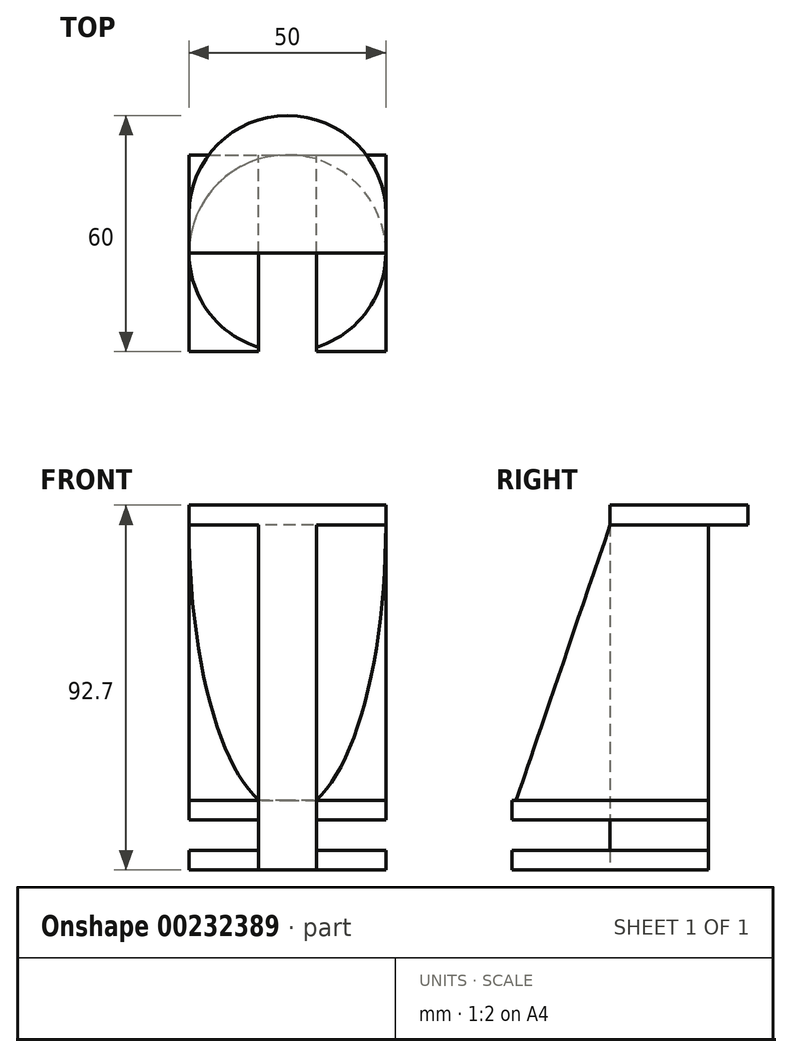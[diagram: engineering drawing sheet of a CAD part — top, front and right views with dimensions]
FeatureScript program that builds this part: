
annotation { "Feature Type Name" : "Feature", "Feature Type Description" : "" }
export const myFeature = defineFeature(function(context is Context, id is Id, definition is map)
    precondition{}
    {
        {
            var Q0;
            Q0=qCreatedBy(makeId("Top.planeOp"),FACE);
            var sketch = newSketch(context, id + "F0", { "sketchPlane" : qUnion([Q0])});
            skLineSegment(sketch, "E0.bottom", {"start": v(0, 0) * mm, "end": v(50, 0) * mm, "construction": true});
            skLineSegment(sketch, "E0.top", {"start": v(0, 50) * mm, "end": v(50, 50) * mm, "construction": true});
            skLineSegment(sketch, "E0.left", {"start": v(0, 0) * mm, "end": v(0, 50) * mm, "construction": true});
            skLineSegment(sketch, "E0.right", {"start": v(50, 0) * mm, "end": v(50, 50) * mm, "construction": true});
            skLineSegment(sketch, "E1.bottom", {"start": v(17.65, 50) * mm, "end": v(32.35, 50) * mm, "construction": true});
            skLineSegment(sketch, "E1.top", {"start": v(17.65, 25) * mm, "end": v(32.35, 25) * mm, "construction": true});
            skLineSegment(sketch, "E1.left", {"start": v(17.65, 50) * mm, "end": v(17.65, 25) * mm, "construction": true});
            skLineSegment(sketch, "E1.right", {"start": v(32.35, 50) * mm, "end": v(32.35, 25) * mm, "construction": true});
            skSolve(sketch);
        }
        {
            var Q0;
            Q0=qCreatedBy(makeId("Top.planeOp"),FACE);
            var sketch = newSketch(context, id + "F1", { "sketchPlane" : qUnion([Q0])});
            skLineSegment(sketch, "E2.0", {"start": v(0, 0) * mm, "end": v(0, 50) * mm});
            skLineSegment(sketch, "E3.0", {"start": v(0, 50) * mm, "end": v(50, 50) * mm});
            skLineSegment(sketch, "E4.0", {"start": v(50, 0) * mm, "end": v(50, 50) * mm});
            skLineSegment(sketch, "E5.0", {"start": v(17.65, 50) * mm, "end": v(17.65, 25) * mm, "construction": true});
            skLineSegment(sketch, "E6.0", {"start": v(17.65, 25) * mm, "end": v(32.35, 25) * mm, "construction": true});
            skLineSegment(sketch, "E7.0", {"start": v(32.35, 50) * mm, "end": v(32.35, 25) * mm, "construction": true});
            skLineSegment(sketch, "E8.0", {"start": v(0, 0) * mm, "end": v(50, 0) * mm, "construction": true});
            skLineSegment(sketch, "E9", {"start": v(0, 0) * mm, "end": v(17.65, 0) * mm});
            skLineSegment(sketch, "E10", {"start": v(17.65, 0) * mm, "end": v(17.65, 25) * mm});
            skLineSegment(sketch, "E11", {"start": v(32.35, 25) * mm, "end": v(32.35, 0) * mm});
            skLineSegment(sketch, "E12", {"start": v(32.35, 0) * mm, "end": v(50, 0) * mm});
            skLineSegment(sketch, "E13", {"start": v(17.65, 25) * mm, "end": v(32.35, 25) * mm});
            skSolve(sketch);
        }
        {
            var Q0;
            Q0 = qSketchRegion(id + "F1", true);
            extrude(context, id + "F2", {"entities" : qUnion([Q0]), "depth" : 5 * mm});
        }
        {
            var Q0;
            Q0=makeQuery(id+"F2.opExtrude","CAP_FACE",FACE,{"disambiguationData":[OSD([sQuery(id+"F1.wireOp",EDGE,"E2.0"),sQuery(id+"F1.wireOp",EDGE,"E3.0"),sQuery(id+"F1.wireOp",EDGE,"E4.0"),sQuery(id+"F1.wireOp",EDGE,"E9"),sQuery(id+"F1.wireOp",EDGE,"E10"),sQuery(id+"F1.wireOp",EDGE,"E11"),sQuery(id+"F1.wireOp",EDGE,"E12"),sQuery(id+"F1.wireOp",EDGE,"E13")])],"isStart":false});
            var sketch = newSketch(context, id + "F3", { "sketchPlane" : qUnion([Q0])});
            skLineSegment(sketch, "E14.bottom", {"start": v(17.65, 25) * mm, "end": v(32.35, 25) * mm});
            skLineSegment(sketch, "E14.top", {"start": v(17.65, 50) * mm, "end": v(32.35, 50) * mm});
            skLineSegment(sketch, "E14.left", {"start": v(17.65, 25) * mm, "end": v(17.65, 50) * mm});
            skLineSegment(sketch, "E14.right", {"start": v(32.35, 25) * mm, "end": v(32.35, 50) * mm});
            skSolve(sketch);
        }
        {
            var Q0;
            Q0 = qSketchRegion(id + "F3", true);
            extrude(context, id + "F4", {"entities" : qUnion([Q0]), "operationType" : NewBodyOperationType.ADD, "depth" : 7.7 * mm});
        }
        {
            var Q0;
            Q0=makeQuery(id+"F4.opExtrude","CAP_FACE",FACE,{"disambiguationData":[OSD([sQuery(id+"F3.wireOp",EDGE,"E14.bottom"),sQuery(id+"F3.wireOp",EDGE,"E14.top"),sQuery(id+"F3.wireOp",EDGE,"E14.left"),sQuery(id+"F3.wireOp",EDGE,"E14.right")])],"isStart":false});
            var sketch = newSketch(context, id + "F5", { "sketchPlane" : qUnion([Q0])});
            skLineSegment(sketch, "E15.0", {"start": v(0, 0) * mm, "end": v(0, 50) * mm});
            skLineSegment(sketch, "E16.0", {"start": v(0, 50) * mm, "end": v(50, 50) * mm});
            skLineSegment(sketch, "E17.0", {"start": v(50, 0) * mm, "end": v(50, 50) * mm});
            skLineSegment(sketch, "E18.0", {"start": v(32.35, 25) * mm, "end": v(32.35, 0) * mm});
            skLineSegment(sketch, "E19.0", {"start": v(17.65, 25) * mm, "end": v(32.35, 25) * mm});
            skLineSegment(sketch, "E20.0", {"start": v(17.65, 0) * mm, "end": v(17.65, 25) * mm});
            skLineSegment(sketch, "E21", {"start": v(0, 0) * mm, "end": v(17.65, 0) * mm});
            skLineSegment(sketch, "E22", {"start": v(32.35, 0) * mm, "end": v(50, 0) * mm});
            skSolve(sketch);
        }
        {
            var Q0;
            Q0 = qSketchRegion(id + "F5", true);
            extrude(context, id + "F6", {"entities" : qUnion([Q0]), "operationType" : NewBodyOperationType.ADD, "depth" : 5 * mm});
        }
        {
            var Q0;
            Q0=makeQuery(id+"F6.opExtrude","CAP_FACE",FACE,{"disambiguationData":[OSD([sQuery(id+"F5.wireOp",EDGE,"E15.0"),sQuery(id+"F5.wireOp",EDGE,"E16.0"),sQuery(id+"F5.wireOp",EDGE,"E17.0"),sQuery(id+"F5.wireOp",EDGE,"E18.0"),sQuery(id+"F5.wireOp",EDGE,"E19.0"),sQuery(id+"F5.wireOp",EDGE,"E20.0"),sQuery(id+"F5.wireOp",EDGE,"E21"),sQuery(id+"F5.wireOp",EDGE,"E22")])],"isStart":false});
            var sketch = newSketch(context, id + "F7", { "sketchPlane" : qUnion([Q0])});
            skArc(sketch, "E23", {"start": v(32.35, 1.1) * mm, "mid": v(25, 50) * mm, "end": v(17.65, 1.1) * mm});
            skLineSegment(sketch, "E24.0", {"start": v(17.65, 25) * mm, "end": v(32.35, 25) * mm});
            skLineSegment(sketch, "E25.0", {"start": v(17.65, 1.1) * mm, "end": v(17.65, 25) * mm});
            skLineSegment(sketch, "E26.0", {"start": v(32.35, 25) * mm, "end": v(32.35, 1.1) * mm});
            skPoint(sketch, "E27.orphan", {"position": v(32.35, 0) * mm});
            skPoint(sketch, "E28.orphan", {"position": v(17.65, 0) * mm});
            skSolve(sketch);
        }
        {
            var Q0;
            Q0 = qSketchRegion(id + "F7", true);
            extrude(context, id + "F8", {"entities" : qUnion([Q0]), "operationType" : NewBodyOperationType.ADD, "depth" : 70 * mm});
        }
        {
            var Q0;
            Q0=makeQuery(id+"F8.opExtrude","CAP_FACE",FACE,{"disambiguationData":[OSD([sQuery(id+"F7.wireOp",EDGE,"E23"),sQuery(id+"F7.wireOp",EDGE,"E24.0"),sQuery(id+"F7.wireOp",EDGE,"E25.0"),sQuery(id+"F7.wireOp",EDGE,"E26.0")])],"isStart":false});
            var sketch = newSketch(context, id + "F9", { "sketchPlane" : qUnion([Q0])});
            skLineSegment(sketch, "E29.bottom", {"start": v(0, 25) * mm, "end": v(50, 25) * mm});
            skLineSegment(sketch, "E29.left", {"start": v(0, 25) * mm, "end": v(0, 35) * mm});
            skLineSegment(sketch, "E29.right", {"start": v(50, 25) * mm, "end": v(50, 35) * mm});
            skArc(sketch, "E30.trimOffspring", {"start": v(50, 35) * mm, "mid": v(25, 60) * mm, "end": v(0, 35) * mm});
            skSolve(sketch);
        }
        {
            var Q0;
            Q0 = qSketchRegion(id + "F9", true);
            extrude(context, id + "F10", {"entities" : qUnion([Q0]), "operationType" : NewBodyOperationType.ADD, "depth" : 5 * mm});
        }
        {
            var Q0;
            Q0=qCreatedBy(makeId("Right.planeOp"),FACE);
            var sketch = newSketch(context, id + "F11", { "sketchPlane" : qUnion([Q0])});
            skLineSegment(sketch, "E31.0", {"start": v(1.1, 87.7) * mm, "end": v(1.1, 17.7) * mm, "construction": true});
            skLineSegment(sketch, "E32.0", {"start": v(25, 87.7) * mm, "end": v(1.1, 87.7) * mm});
            skLineSegment(sketch, "E33", {"start": v(1.1, 17.7) * mm, "end": v(25, 87.7) * mm});
            skLineSegment(sketch, "E34", {"start": v(1.1, 87.7) * mm, "end": v(1.1, 17.7) * mm});
            skSolve(sketch);
        }
        {
            var Q0;
            Q0 = qSketchRegion(id + "F11", true);
            extrude(context, id + "F12", {"entities" : qUnion([Q0]), "operationType" : NewBodyOperationType.REMOVE, "endBound" : BoundingType.THROUGH_ALL, "depth" : 25 * mm});
        }
    });
